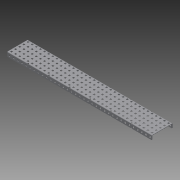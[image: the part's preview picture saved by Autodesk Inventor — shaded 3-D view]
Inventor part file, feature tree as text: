
AUTODESK INVENTOR PART (.ipt)
format: ipt  version: 2015 (Build 190159000, 159)  size: 3,629,568 bytes
history: native  units: in
note: dims shown in document units (in); Inventor stores cm internally (conversion verified against a paired STEP export)
features: other x247, extrude x245, pattern_linear x4, sketch x3, imported_body x1
ambient origin geometry x8: Origin, YZ Plane, XZ Plane, XY Plane, X Axis, Y Axis, Z Axis, Center Point
bodies: Body1 (feature_tree), Body2 (feature_tree), Body3 (feature_tree), Body4 (feature_tree), Body5 (feature_tree), Body6 (feature_tree), Body7 (feature_tree), Body8 (feature_tree), Body9 (feature_tree), Body10 (feature_tree), Body11 (feature_tree), Body12 (feature_tree), Body13 (feature_tree), Body14 (feature_tree), Body15 (feature_tree), Body16 (feature_tree), Body17 (feature_tree), Body18 (feature_tree), Body19 (feature_tree), Body20 (feature_tree), Body21 (feature_tree), Body22 (feature_tree), Body23 (feature_tree), Body24 (feature_tree), Body25 (feature_tree), Body26 (feature_tree), Body27 (feature_tree), Body28 (feature_tree), Body29 (feature_tree), Body30 (feature_tree), Body31 (feature_tree), Body32 (feature_tree), Body33 (feature_tree), Body34 (feature_tree), Body35 (feature_tree), Body36 (feature_tree), Body37 (feature_tree), Body38 (feature_tree), Body39 (feature_tree), Body40 (feature_tree), Body41 (feature_tree), Body42 (feature_tree), Body43 (feature_tree), Body44 (feature_tree), Body45 (feature_tree), Body46 (feature_tree), Body47 (feature_tree), Body48 (feature_tree), Body49 (feature_tree), Body50 (feature_tree), Body51 (feature_tree), Body52 (feature_tree), Body53 (feature_tree), Body54 (feature_tree), Body55 (feature_tree), Body56 (feature_tree), Body57 (feature_tree), Body58 (feature_tree), Body59 (feature_tree), Body60 (feature_tree), Body61 (feature_tree), Body62 (feature_tree), Body63 (feature_tree), Body64 (feature_tree), Body65 (feature_tree), Body66 (feature_tree), Body67 (feature_tree), Body68 (feature_tree), Body69 (feature_tree), Body70 (feature_tree), Body71 (feature_tree), Body72 (feature_tree), Body73 (feature_tree), Body74 (feature_tree), Body75 (feature_tree), Body76 (feature_tree), Body77 (feature_tree), Body78 (feature_tree), Body79 (feature_tree), Body80 (feature_tree), Body81 (feature_tree), Body82 (feature_tree), Body83 (feature_tree), Body84 (feature_tree), Body85 (feature_tree), Body86 (feature_tree), Body87 (feature_tree), Body88 (feature_tree), Body89 (feature_tree), Body90 (feature_tree), Body91 (feature_tree), Body92 (feature_tree), Body93 (feature_tree), Body94 (feature_tree), Body95 (feature_tree), Body96 (feature_tree), Body97 (feature_tree), Body98 (feature_tree), Body99 (feature_tree), Body100 (feature_tree), Body101 (feature_tree), Body102 (feature_tree), Body103 (feature_tree), Body104 (feature_tree), Body105 (feature_tree), Body106 (feature_tree), Body107 (feature_tree), Body108 (feature_tree), Body109 (feature_tree), Body110 (feature_tree), Body111 (feature_tree), Body112 (feature_tree), Body113 (feature_tree), Body114 (feature_tree), Body115 (feature_tree), Body116 (feature_tree), Body117 (feature_tree), Body118 (feature_tree), Body119 (feature_tree), Body120 (feature_tree), Body121 (feature_tree), Body122 (feature_tree), Body123 (feature_tree), Body124 (feature_tree), Body125 (feature_tree), Body126 (feature_tree), Body127 (feature_tree), Body128 (feature_tree), Body129 (feature_tree), Body130 (feature_tree), Body131 (feature_tree), Body132 (feature_tree), Body133 (feature_tree), Body134 (feature_tree), Body135 (feature_tree), Body136 (feature_tree), Body137 (feature_tree), Body138 (feature_tree), Body139 (feature_tree), Body140 (feature_tree), Body141 (feature_tree), Body142 (feature_tree), Body143 (feature_tree), Body144 (feature_tree), Body145 (feature_tree), Body146 (feature_tree), Body147 (feature_tree), Body148 (feature_tree), Body149 (feature_tree), Body150 (feature_tree), Body151 (feature_tree), Body152 (feature_tree), Body153 (feature_tree), Body154 (feature_tree), Body155 (feature_tree), Body156 (feature_tree), Body157 (feature_tree), Body158 (feature_tree), Body159 (feature_tree), Body160 (feature_tree), Body161 (feature_tree), Body162 (feature_tree), Body163 (feature_tree), Body164 (feature_tree), Body165 (feature_tree), Body166 (feature_tree), Body167 (feature_tree), Body168 (feature_tree), Body169 (feature_tree), Body170 (feature_tree), Body171 (feature_tree), Body172 (feature_tree), Body173 (feature_tree), Body174 (feature_tree), Body175 (feature_tree), Body176 (feature_tree), Body177 (feature_tree), Body178 (feature_tree), Body179 (feature_tree), Body180 (feature_tree), Body181 (feature_tree), Body182 (feature_tree), Body183 (feature_tree), Body184 (feature_tree), Body185 (feature_tree), Body186 (feature_tree), Body187 (feature_tree), Body188 (feature_tree), Body189 (feature_tree), Body190 (feature_tree), Body191 (feature_tree), Body192 (feature_tree), Body193 (feature_tree), Body194 (feature_tree), Body195 (feature_tree), Body196 (feature_tree), Body197 (feature_tree), Body198 (feature_tree), Body199 (feature_tree), Body200 (feature_tree), Body201 (feature_tree), Body202 (feature_tree), Body203 (feature_tree), Body204 (feature_tree), Body205 (feature_tree), Body206 (feature_tree), Body207 (feature_tree), Body208 (feature_tree), Body209 (feature_tree), Body210 (feature_tree), Body211 (feature_tree), Body212 (feature_tree), Body213 (feature_tree), Body214 (feature_tree), Body215 (feature_tree), Body216 (feature_tree), Body217 (feature_tree), Body218 (feature_tree), Body219 (feature_tree), Body220 (feature_tree), Body221 (feature_tree), Body222 (feature_tree), Body223 (feature_tree), Body224 (feature_tree), Body225 (feature_tree), Body226 (feature_tree), Body227 (feature_tree), Body228 (feature_tree), Body229 (feature_tree), Body230 (feature_tree), Body231 (feature_tree), Body232 (feature_tree), Body233 (feature_tree), Body234 (feature_tree), Body235 (feature_tree), Body236 (feature_tree), Body237 (feature_tree), Body238 (feature_tree), Body239 (feature_tree), Body240 (feature_tree), Body241 (feature_tree), Body242 (feature_tree), Body243 (feature_tree), Body244 (feature_tree), Body245 (feature_tree), Body246 (feature_tree)
feature tree (500):
  parser-record x1  (decoder bookkeeping rows leaked as tree rows — omitted from the tree; the rows remain in map.json)
  other  "VL-CHAN-151-35 RevA1"
  pattern_linear  "Rectangular Pattern1"  Count1=5 Spacing1=0.5in
  pattern_linear  "Rectangular Pattern2"  Count1=35 Spacing1=0.5in
  pattern_linear  "Rectangular Pattern3"  Spacing1=0.0in  [1 undecoded]
  pattern_linear  "Rectangular Pattern4"  Spacing1=0.0in  [1 undecoded]
  imported_body  "Base1"
  sketch  "Sketch1"  dims[d0=0.05in d1=0.0in]
  other  "Srf1"
  other  "Srf2"
  other  "Srf3"
  other  "Srf4"
  other  "Srf5"
  other  "Srf10"
  other  "Srf15"
  other  "Srf20"
  other  "Srf25"
  other  "Srf30"
  other  "Srf35"
  other  "Srf40"
  other  "Srf45"
  other  "Srf50"
  other  "Srf55"
  other  "Srf60"
  other  "Srf65"
  other  "Srf70"
  other  "Srf75"
  other  "Srf80"
  other  "Srf85"
  other  "Srf90"
  other  "Srf95"
  other  "Srf100"
  other  "Srf105"
  other  "Srf110"
  other  "Srf115"
  other  "Srf120"
  other  "Srf125"
  other  "Srf130"
  other  "Srf135"
  other  "Srf140"
  other  "Srf145"
  other  "Srf150"
  other  "Srf155"
  other  "Srf160"
  other  "Srf165"
  other  "Srf170"
  other  "Srf175"
  other  "Srf6"
  other  "Srf11"
  other  "Srf16"
  other  "Srf21"
  other  "Srf26"
  other  "Srf31"
  other  "Srf36"
  other  "Srf41"
  other  "Srf46"
  other  "Srf51"
  other  "Srf56"
  other  "Srf61"
  other  "Srf66"
  other  "Srf71"
  other  "Srf76"
  other  "Srf81"
  other  "Srf86"
  other  "Srf91"
  other  "Srf96"
  other  "Srf101"
  other  "Srf106"
  other  "Srf111"
  other  "Srf116"
  other  "Srf121"
  other  "Srf126"
  other  "Srf131"
  other  "Srf136"
  other  "Srf141"
  other  "Srf146"
  other  "Srf151"
  other  "Srf156"
  other  "Srf161"
  other  "Srf166"
  other  "Srf171"
  other  "Srf7"
  other  "Srf12"
  other  "Srf17"
  other  "Srf22"
  other  "Srf27"
  other  "Srf32"
  other  "Srf37"
  other  "Srf42"
  other  "Srf47"
  other  "Srf52"
  other  "Srf57"
  other  "Srf62"
  other  "Srf67"
  other  "Srf72"
  other  "Srf77"
  other  "Srf82"
  other  "Srf87"
  other  "Srf92"
  other  "Srf97"
  other  "Srf102"
  other  "Srf107"
  other  "Srf112"
  other  "Srf117"
  other  "Srf122"
  other  "Srf127"
  other  "Srf132"
  other  "Srf137"
  other  "Srf142"
  other  "Srf147"
  other  "Srf152"
  other  "Srf157"
  other  "Srf162"
  other  "Srf167"
  other  "Srf172"
  other  "Srf8"
  other  "Srf13"
  other  "Srf18"
  other  "Srf23"
  other  "Srf28"
  other  "Srf33"
  other  "Srf38"
  other  "Srf43"
  other  "Srf48"
  other  "Srf53"
  other  "Srf58"
  other  "Srf63"
  other  "Srf68"
  other  "Srf73"
  other  "Srf78"
  other  "Srf83"
  other  "Srf88"
  other  "Srf93"
  other  "Srf98"
  other  "Srf103"
  other  "Srf108"
  other  "Srf113"
  other  "Srf118"
  other  "Srf123"
  other  "Srf128"
  other  "Srf133"
  other  "Srf138"
  other  "Srf143"
  other  "Srf148"
  other  "Srf153"
  other  "Srf158"
  other  "Srf163"
  other  "Srf168"
  other  "Srf173"
  other  "Srf9"
  other  "Srf14"
  other  "Srf19"
  other  "Srf24"
  other  "Srf29"
  other  "Srf34"
  other  "Srf39"
  other  "Srf44"
  other  "Srf49"
  other  "Srf54"
  other  "Srf59"
  other  "Srf64"
  other  "Srf69"
  other  "Srf74"
  other  "Srf79"
  other  "Srf84"
  other  "Srf89"
  other  "Srf94"
  other  "Srf99"
  other  "Srf104"
  other  "Srf109"
  other  "Srf114"
  other  "Srf119"
  other  "Srf124"
  other  "Srf129"
  other  "Srf134"
  other  "Srf139"
  other  "Srf144"
  other  "Srf149"
  other  "Srf154"
  other  "Srf159"
  other  "Srf164"
  other  "Srf169"
  other  "Srf174"
  sketch  "Sketch2"  dims[d2=0.0in]
  other  "Srf176"
  other  "Srf177"
  other  "Srf178"
  other  "Srf179"
  other  "Srf180"
  other  "Srf181"
  other  "Srf182"
  other  "Srf183"
  other  "Srf184"
  other  "Srf185"
  other  "Srf186"
  other  "Srf187"
  other  "Srf188"
  other  "Srf189"
  other  "Srf190"
  other  "Srf191"
  other  "Srf192"
  other  "Srf193"
  other  "Srf194"
  other  "Srf195"
  other  "Srf196"
  other  "Srf197"
  other  "Srf198"
  other  "Srf199"
  other  "Srf200"
  other  "Srf201"
  other  "Srf202"
  other  "Srf203"
  other  "Srf204"
  other  "Srf205"
  other  "Srf206"
  other  "Srf207"
  other  "Srf208"
  other  "Srf209"
  other  "Srf210"
  sketch  "Sketch3"  dims[d3=0.0in d4=1.9685in d6=0.5in d7=13.7795in d9=0.5in d10=0.0in d11=0.0in d12=0.0in d13=0.0in d14=0.0in d15=0.0in d16=0.0in d17=0.0in d18=0.0in d19=0.0in d20=0.0in d21=0.0in d22=0.0in d23=0.0in d24=0.0in d25=0.0in d26=0.0in d27=0.0in d28=0.0in d29=0.0in d30=0.0in d31=0.0in d32=0.0in d33=0.0in d34=0.0in d35=0.0in d36=0.0in d37=0.0in d38=0.0in d39=0.0in d40=0.0in d41=0.0in d42=0.0in d43=0.0in d44=0.0in d45=0.0in d46=0.0in d47=0.0in d48=0.0in d49=0.0in d50=0.0in d51=0.0in d52=0.0in d53=0.0in d54=0.0in d55=0.0in d56=0.0in d57=0.0in d58=0.0in d59=0.0in d60=0.0in d61=0.0in d62=0.0in d63=0.0in d64=0.0in d65=0.0in d66=0.0in d67=0.0in d68=0.0in d69=0.0in d70=0.0in d71=0.0in d72=0.0in d73=0.0in d74=0.0in d75=0.0in d76=0.0in d77=0.0in d78=0.0in d79=0.0in d80=0.0in d81=0.0in d82=0.0in d83=0.0in d84=0.0in d85=0.0in d86=0.0in d87=0.0in d88=0.0in d89=0.0in d90=0.0in d91=0.0in d92=0.0in d93=0.0in d94=0.0in d95=0.0in d96=0.0in d97=0.0in d98=0.0in d99=0.0in d100=0.0in d101=0.0in d102=0.0in d103=0.0in d104=0.0in d105=0.0in d106=0.0in d107=0.0in d108=0.0in d109=0.0in d110=0.0in d111=0.0in d112=0.0in d113=0.0in d114=0.0in d115=0.0in d116=0.0in d117=0.0in d118=0.0in d119=0.0in d120=0.0in d121=0.0in d122=0.0in d123=0.0in d124=0.0in d125=0.0in d126=0.0in d127=0.0in d128=0.0in d129=0.0in d130=0.0in d131=0.0in d132=0.0in d133=0.0in d134=0.0in d135=0.0in d136=0.0in d137=0.0in d138=0.0in d139=0.0in d140=0.0in d141=0.0in d142=0.0in d143=0.0in d144=0.0in d145=0.0in d146=0.0in d147=0.0in d148=0.0in d149=0.0in d150=0.0in d151=0.0in d152=0.0in d153=0.0in d154=0.0in d155=0.0in d156=0.0in d157=0.0in d158=0.0in d159=0.0in d160=0.0in d161=0.0in d162=0.0in d163=0.0in d164=0.0in d165=0.0in d166=0.0in d167=0.0in d168=0.0in d169=0.0in d170=0.0in d171=0.0in d172=0.0in d173=0.0in d174=0.0in d175=0.0in d176=0.0in d177=0.0in d178=0.0in d179=0.0in d180=0.0in d181=0.0in d182=0.0in d183=0.0in d184=0.0in d185=0.0in d186=0.0in d187=0.0in d188=0.0in d189=0.0in d190=0.0in d191=0.0in d192=0.0in d193=0.0in d194=0.0in d195=0.0in d196=0.0in d197=0.0in d198=0.0in d199=0.0in d200=0.0in d201=0.0in d202=0.0in d203=0.0in d204=0.0in d205=0.0in d206=0.0in d207=0.0in d208=0.0in d209=0.0in d210=0.0in d211=0.0in d212=0.0in d213=0.0in d214=0.0in d215=0.0in d216=0.0in d217=0.0in d218=0.0in d219=0.0in d220=0.0in d221=0.0in d222=0.0in d223=0.0in d224=0.0in d225=0.0in d226=0.0in d227=0.0in d228=0.0in d229=0.0in d230=0.0in d231=0.0in d232=0.0in d233=0.0in d234=0.0in d235=0.0in d236=0.0in d237=0.0in d238=0.0in d239=0.0in d240=0.0in d241=0.0in d242=0.0in d243=0.0in d244=0.0in d245=0.0in d246=0.0in d247=0.0in d248=0.0in d249=0.0in d250=0.0in d251=0.0in d252=0.0in d253=0.0in d254=0.0in d255=0.0in d256=0.0in d257=0.0in d258=0.0in d259=0.0in d260=0.0in d261=0.0in d262=0.0in d263=0.0in d264=0.0in d265=0.0in d266=0.0in d267=0.0in d268=0.0in d269=0.0in d270=0.0in d271=0.0in d272=0.0in d273=0.0in d274=0.0in d275=0.0in d276=0.0in d277=0.0in d278=0.0in d279=0.0in d280=0.0in d281=0.0in d282=0.0in d283=0.0in d284=0.0in d285=0.0in d286=0.0in d287=0.0in d288=0.0in d289=0.0in d290=0.0in d291=0.0in d292=0.0in d293=0.0in d294=0.0in d295=0.0in d296=0.0in d297=0.0in d298=0.0in d299=0.0in d300=0.0in d301=0.0in d302=0.0in d303=0.0in d304=0.0in d305=0.0in d306=0.0in d307=0.0in d308=0.0in d309=0.0in d310=0.0in d311=0.0in d312=0.0in d313=0.0in d314=0.0in d315=0.0in d316=0.0in d317=0.0in d318=0.0in d319=0.0in d320=0.0in d321=0.0in d322=0.0in d323=0.0in d324=0.0in d325=0.0in d326=0.0in d327=0.0in d328=0.0in d329=0.0in d330=0.0in d331=0.0in d332=0.0in d333=0.0in d334=0.0in d335=0.0in d336=0.0in d337=0.0in d338=0.0in d339=0.0in d340=0.0in d341=0.0in d342=0.0in d343=0.0in d344=0.0in d345=0.0in d346=0.0in d347=0.0in d348=0.0in d349=0.0in d350=0.0in d351=0.0in d352=0.0in d353=0.0in d354=0.0in d355=0.0in d356=0.0in d357=0.05in d358=0.0in d359=13.7795in d361=0.5in d362=0.0in d363=0.0in d364=0.0in d365=0.0in d366=0.0in d367=0.0in d368=0.0in d369=0.0in d370=0.0in d371=0.0in d372=0.0in d373=0.0in d374=0.0in d375=0.0in d376=0.0in d377=0.0in d378=0.0in d379=0.0in d380=0.0in d381=0.0in d382=0.0in d383=0.0in d384=0.0in d385=0.0in d386=0.0in d387=0.0in d388=0.0in d389=0.0in d390=0.0in d391=0.0in d392=0.0in d393=0.0in d394=0.0in d395=0.0in d396=0.0in d397=0.0in d398=0.0in d399=0.0in d400=0.0in d401=0.0in d402=0.0in d403=0.0in d404=0.0in d405=0.0in d406=0.0in d407=0.0in d408=0.0in d409=0.0in d410=0.0in d411=0.0in d412=0.0in d413=0.0in d414=0.0in d415=0.0in d416=0.0in d417=0.0in d418=0.0in d419=0.0in d420=0.0in d421=0.0in d422=0.0in d423=0.0in d424=0.0in d425=0.0in d426=0.0in d427=0.0in d428=0.0in d429=0.0in d430=0.0in d431=0.0in d432=0.05in d433=0.0in d434=13.7795in d436=0.5in d437=0.0in d438=0.0in d439=0.0in d440=0.0in d441=0.0in d442=0.0in d443=0.0in d444=0.0in d445=0.0in d446=0.0in d447=0.0in d448=0.0in d449=0.0in d450=0.0in d451=0.0in d452=0.0in d453=0.0in d454=0.0in d455=0.0in d456=0.0in d457=0.0in d458=0.0in d459=0.0in d460=0.0in d461=0.0in d462=0.0in d463=0.0in d464=0.0in d465=0.0in d466=0.0in d467=0.0in d468=0.0in d469=0.0in d470=0.0in d471=0.0in d472=0.0in d473=0.0in d474=0.0in d475=0.0in d476=0.0in d477=0.0in d478=0.0in d479=0.0in d480=0.0in d481=0.0in d482=0.0in d483=0.0in d484=0.0in d485=0.0in d486=0.0in d487=0.0in d488=0.0in d489=0.0in d490=0.0in d491=0.0in d492=0.0in d493=0.0in d494=0.0in d495=0.0in d496=0.0in d497=0.0in d498=0.0in d499=0.0in d500=0.0in d501=0.0in d502=0.0in d503=0.0in d504=0.0in d505=0.0in d506=0.0in]
  other  "Srf211"
  other  "Srf212"
  other  "Srf213"
  other  "Srf214"
  other  "Srf215"
  other  "Srf216"
  other  "Srf217"
  other  "Srf218"
  other  "Srf219"
  other  "Srf220"
  other  "Srf221"
  other  "Srf222"
  other  "Srf223"
  other  "Srf224"
  other  "Srf225"
  other  "Srf226"
  other  "Srf227"
  other  "Srf228"
  other  "Srf229"
  other  "Srf230"
  other  "Srf231"
  other  "Srf232"
  other  "Srf233"
  other  "Srf234"
  other  "Srf235"
  other  "Srf236"
  other  "Srf237"
  other  "Srf238"
  other  "Srf239"
  other  "Srf240"
  other  "Srf241"
  other  "Srf242"
  other  "Srf243"
  other  "Srf244"
  other  "Srf245"
  extrude  "ExtrusionSrf1"  TaperAngle=0.0deg  [1 undecoded]
  extrude  "ExtrusionSrf176"  TaperAngle=0.0deg  [1 undecoded]
  extrude  "ExtrusionSrf211"  TaperAngle=0.0deg  [1 undecoded]
  extrude  "ExtrusionSrf2"  TaperAngle=0.0deg  [1 undecoded]
  extrude  "ExtrusionSrf3"  TaperAngle=0.0deg  [1 undecoded]
  extrude  "ExtrusionSrf4"  TaperAngle=0.0deg  [1 undecoded]
  extrude  "ExtrusionSrf5"  TaperAngle=0.0deg  [1 undecoded]
  extrude  "ExtrusionSrf6"  TaperAngle=0.0deg  [1 undecoded]
  extrude  "ExtrusionSrf7"  TaperAngle=0.0deg  [1 undecoded]
  extrude  "ExtrusionSrf8"  TaperAngle=0.0deg  [1 undecoded]
  extrude  "ExtrusionSrf9"  TaperAngle=0.0deg  [1 undecoded]
  extrude  "ExtrusionSrf10"  TaperAngle=0.0deg  [1 undecoded]
  extrude  "ExtrusionSrf11"  TaperAngle=0.0deg  [1 undecoded]
  extrude  "ExtrusionSrf12"  TaperAngle=0.0deg  [1 undecoded]
  extrude  "ExtrusionSrf13"  TaperAngle=0.0deg  [1 undecoded]
  extrude  "ExtrusionSrf14"  TaperAngle=0.0deg  [1 undecoded]
  extrude  "ExtrusionSrf15"  TaperAngle=0.0deg  [1 undecoded]
  extrude  "ExtrusionSrf16"  TaperAngle=0.0deg  [1 undecoded]
  extrude  "ExtrusionSrf17"  TaperAngle=0.0deg  [1 undecoded]
  extrude  "ExtrusionSrf18"  TaperAngle=0.0deg  [1 undecoded]
  extrude  "ExtrusionSrf19"  TaperAngle=0.0deg  [1 undecoded]
  extrude  "ExtrusionSrf20"  TaperAngle=0.0deg  [1 undecoded]
  extrude  "ExtrusionSrf21"  TaperAngle=0.0deg  [1 undecoded]
  extrude  "ExtrusionSrf22"  TaperAngle=0.0deg  [1 undecoded]
  extrude  "ExtrusionSrf23"  TaperAngle=0.0deg  [1 undecoded]
  extrude  "ExtrusionSrf24"  TaperAngle=0.0deg  [1 undecoded]
  extrude  "ExtrusionSrf25"  TaperAngle=0.0deg  [1 undecoded]
  extrude  "ExtrusionSrf26"  TaperAngle=0.0deg  [1 undecoded]
  extrude  "ExtrusionSrf27"  TaperAngle=0.0deg  [1 undecoded]
  extrude  "ExtrusionSrf28"  TaperAngle=0.0deg  [1 undecoded]
  extrude  "ExtrusionSrf29"  TaperAngle=0.0deg  [1 undecoded]
  extrude  "ExtrusionSrf30"  TaperAngle=0.0deg  [1 undecoded]
  extrude  "ExtrusionSrf31"  TaperAngle=0.0deg  [1 undecoded]
  extrude  "ExtrusionSrf32"  TaperAngle=0.0deg  [1 undecoded]
  extrude  "ExtrusionSrf33"  TaperAngle=0.0deg  [1 undecoded]
  extrude  "ExtrusionSrf34"  TaperAngle=0.0deg  [1 undecoded]
  extrude  "ExtrusionSrf35"  TaperAngle=0.0deg  [1 undecoded]
  extrude  "ExtrusionSrf36"  TaperAngle=0.0deg  [1 undecoded]
  extrude  "ExtrusionSrf37"  TaperAngle=0.0deg  [1 undecoded]
  extrude  "ExtrusionSrf38"  TaperAngle=0.0deg  [1 undecoded]
  extrude  "ExtrusionSrf39"  TaperAngle=0.0deg  [1 undecoded]
  extrude  "ExtrusionSrf40"  TaperAngle=0.0deg  [1 undecoded]
  extrude  "ExtrusionSrf41"  TaperAngle=0.0deg  [1 undecoded]
  extrude  "ExtrusionSrf42"  TaperAngle=0.0deg  [1 undecoded]
  extrude  "ExtrusionSrf43"  TaperAngle=0.0deg  [1 undecoded]
  extrude  "ExtrusionSrf44"  TaperAngle=0.0deg  [1 undecoded]
  extrude  "ExtrusionSrf45"  TaperAngle=0.0deg  [1 undecoded]
  extrude  "ExtrusionSrf46"  TaperAngle=0.0deg  [1 undecoded]
  extrude  "ExtrusionSrf47"  TaperAngle=0.0deg  [1 undecoded]
  extrude  "ExtrusionSrf48"  TaperAngle=0.0deg  [1 undecoded]
  extrude  "ExtrusionSrf49"  TaperAngle=0.0deg  [1 undecoded]
  extrude  "ExtrusionSrf50"  TaperAngle=0.0deg  [1 undecoded]
  extrude  "ExtrusionSrf51"  TaperAngle=0.0deg  [1 undecoded]
  extrude  "ExtrusionSrf52"  TaperAngle=0.0deg  [1 undecoded]
  extrude  "ExtrusionSrf53"  TaperAngle=0.0deg  [1 undecoded]
  extrude  "ExtrusionSrf54"  TaperAngle=0.0deg  [1 undecoded]
  extrude  "ExtrusionSrf55"  TaperAngle=0.0deg  [1 undecoded]
  extrude  "ExtrusionSrf56"  TaperAngle=0.0deg  [1 undecoded]
  extrude  "ExtrusionSrf57"  TaperAngle=0.0deg  [1 undecoded]
  extrude  "ExtrusionSrf58"  TaperAngle=0.0deg  [1 undecoded]
  extrude  "ExtrusionSrf59"  TaperAngle=0.0deg  [1 undecoded]
  extrude  "ExtrusionSrf60"  TaperAngle=0.0deg  [1 undecoded]
  extrude  "ExtrusionSrf61"  TaperAngle=0.0deg  [1 undecoded]
  extrude  "ExtrusionSrf62"  TaperAngle=0.0deg  [1 undecoded]
  extrude  "ExtrusionSrf63"  TaperAngle=0.0deg  [1 undecoded]
  extrude  "ExtrusionSrf64"  TaperAngle=0.0deg  [1 undecoded]
  extrude  "ExtrusionSrf65"  TaperAngle=0.0deg  [1 undecoded]
  extrude  "ExtrusionSrf66"  TaperAngle=0.0deg  [1 undecoded]
  extrude  "ExtrusionSrf67"  TaperAngle=0.0deg  [1 undecoded]
  extrude  "ExtrusionSrf68"  TaperAngle=0.0deg  [1 undecoded]
  extrude  "ExtrusionSrf69"  TaperAngle=0.0deg  [1 undecoded]
  extrude  "ExtrusionSrf70"  TaperAngle=0.0deg  [1 undecoded]
  extrude  "ExtrusionSrf71"  TaperAngle=0.0deg  [1 undecoded]
  extrude  "ExtrusionSrf72"  TaperAngle=0.0deg  [1 undecoded]
  extrude  "ExtrusionSrf73"  TaperAngle=0.0deg  [1 undecoded]
  extrude  "ExtrusionSrf74"  TaperAngle=0.0deg  [1 undecoded]
  extrude  "ExtrusionSrf75"  TaperAngle=0.0deg  [1 undecoded]
  extrude  "ExtrusionSrf76"  TaperAngle=0.0deg  [1 undecoded]
  extrude  "ExtrusionSrf77"  TaperAngle=0.0deg  [1 undecoded]
  extrude  "ExtrusionSrf78"  TaperAngle=0.0deg  [1 undecoded]
  extrude  "ExtrusionSrf79"  TaperAngle=0.0deg  [1 undecoded]
  extrude  "ExtrusionSrf80"  TaperAngle=0.0deg  [1 undecoded]
  extrude  "ExtrusionSrf81"  TaperAngle=0.0deg  [1 undecoded]
  extrude  "ExtrusionSrf82"  TaperAngle=0.0deg  [1 undecoded]
  extrude  "ExtrusionSrf83"  TaperAngle=0.0deg  [1 undecoded]
  extrude  "ExtrusionSrf84"  TaperAngle=0.0deg  [1 undecoded]
  extrude  "ExtrusionSrf85"  TaperAngle=0.0deg  [1 undecoded]
  extrude  "ExtrusionSrf86"  TaperAngle=0.0deg  [1 undecoded]
  extrude  "ExtrusionSrf87"  TaperAngle=0.0deg  [1 undecoded]
  extrude  "ExtrusionSrf88"  TaperAngle=0.0deg  [1 undecoded]
  extrude  "ExtrusionSrf89"  TaperAngle=0.0deg  [1 undecoded]
  extrude  "ExtrusionSrf90"  TaperAngle=0.0deg  [1 undecoded]
  extrude  "ExtrusionSrf91"  TaperAngle=0.0deg  [1 undecoded]
  extrude  "ExtrusionSrf92"  TaperAngle=0.0deg  [1 undecoded]
  extrude  "ExtrusionSrf93"  TaperAngle=0.0deg  [1 undecoded]
  extrude  "ExtrusionSrf94"  TaperAngle=0.0deg  [1 undecoded]
  extrude  "ExtrusionSrf95"  TaperAngle=0.0deg  [1 undecoded]
  extrude  "ExtrusionSrf96"  TaperAngle=0.0deg  [1 undecoded]
  extrude  "ExtrusionSrf97"  TaperAngle=0.0deg  [1 undecoded]
  extrude  "ExtrusionSrf98"  TaperAngle=0.0deg  [1 undecoded]
  extrude  "ExtrusionSrf99"  TaperAngle=0.0deg  [1 undecoded]
  extrude  "ExtrusionSrf100"  TaperAngle=0.0deg  [1 undecoded]
  extrude  "ExtrusionSrf101"  TaperAngle=0.0deg  [1 undecoded]
  extrude  "ExtrusionSrf102"  TaperAngle=0.0deg  [1 undecoded]
  extrude  "ExtrusionSrf103"  TaperAngle=0.0deg  [1 undecoded]
  extrude  "ExtrusionSrf104"  TaperAngle=0.0deg  [1 undecoded]
  extrude  "ExtrusionSrf105"  TaperAngle=0.0deg  [1 undecoded]
  extrude  "ExtrusionSrf106"  TaperAngle=0.0deg  [1 undecoded]
  extrude  "ExtrusionSrf107"  TaperAngle=0.0deg  [1 undecoded]
  extrude  "ExtrusionSrf108"  TaperAngle=0.0deg  [1 undecoded]
  extrude  "ExtrusionSrf109"  TaperAngle=0.0deg  [1 undecoded]
  extrude  "ExtrusionSrf110"  TaperAngle=0.0deg  [1 undecoded]
  extrude  "ExtrusionSrf111"  TaperAngle=0.0deg  [1 undecoded]
  extrude  "ExtrusionSrf112"  TaperAngle=0.0deg  [1 undecoded]
  extrude  "ExtrusionSrf113"  TaperAngle=0.0deg  [1 undecoded]
  extrude  "ExtrusionSrf114"  TaperAngle=0.0deg  [1 undecoded]
  extrude  "ExtrusionSrf115"  TaperAngle=0.0deg  [1 undecoded]
  extrude  "ExtrusionSrf116"  TaperAngle=0.0deg  [1 undecoded]
  extrude  "ExtrusionSrf117"  TaperAngle=0.0deg  [1 undecoded]
  extrude  "ExtrusionSrf118"  TaperAngle=0.0deg  [1 undecoded]
  extrude  "ExtrusionSrf119"  TaperAngle=0.0deg  [1 undecoded]
  extrude  "ExtrusionSrf120"  TaperAngle=0.0deg  [1 undecoded]
  extrude  "ExtrusionSrf121"  TaperAngle=0.0deg  [1 undecoded]
  extrude  "ExtrusionSrf122"  TaperAngle=0.0deg  [1 undecoded]
  extrude  "ExtrusionSrf123"  TaperAngle=0.0deg  [1 undecoded]
  extrude  "ExtrusionSrf124"  TaperAngle=0.0deg  [1 undecoded]
  extrude  "ExtrusionSrf125"  TaperAngle=0.0deg  [1 undecoded]
  extrude  "ExtrusionSrf126"  TaperAngle=0.0deg  [1 undecoded]
  extrude  "ExtrusionSrf127"  TaperAngle=0.0deg  [1 undecoded]
  extrude  "ExtrusionSrf128"  TaperAngle=0.0deg  [1 undecoded]
  extrude  "ExtrusionSrf129"  TaperAngle=0.0deg  [1 undecoded]
  extrude  "ExtrusionSrf130"  TaperAngle=0.0deg  [1 undecoded]
  extrude  "ExtrusionSrf131"  TaperAngle=0.0deg  [1 undecoded]
  extrude  "ExtrusionSrf132"  TaperAngle=0.0deg  [1 undecoded]
  extrude  "ExtrusionSrf133"  TaperAngle=0.0deg  [1 undecoded]
  extrude  "ExtrusionSrf134"  TaperAngle=0.0deg  [1 undecoded]
  extrude  "ExtrusionSrf135"  TaperAngle=0.0deg  [1 undecoded]
  extrude  "ExtrusionSrf136"  TaperAngle=0.0deg  [1 undecoded]
  extrude  "ExtrusionSrf137"  TaperAngle=0.0deg  [1 undecoded]
  extrude  "ExtrusionSrf138"  TaperAngle=0.0deg  [1 undecoded]
  extrude  "ExtrusionSrf139"  TaperAngle=0.0deg  [1 undecoded]
  extrude  "ExtrusionSrf140"  TaperAngle=0.0deg  [1 undecoded]
  extrude  "ExtrusionSrf141"  TaperAngle=0.0deg  [1 undecoded]
  extrude  "ExtrusionSrf142"  TaperAngle=0.0deg  [1 undecoded]
  extrude  "ExtrusionSrf143"  TaperAngle=0.0deg  [1 undecoded]
  extrude  "ExtrusionSrf144"  TaperAngle=0.0deg  [1 undecoded]
  extrude  "ExtrusionSrf145"  TaperAngle=0.0deg  [1 undecoded]
  extrude  "ExtrusionSrf146"  TaperAngle=0.0deg  [1 undecoded]
  extrude  "ExtrusionSrf147"  TaperAngle=0.0deg  [1 undecoded]
  extrude  "ExtrusionSrf148"  TaperAngle=0.0deg  [1 undecoded]
  extrude  "ExtrusionSrf149"  TaperAngle=0.0deg  [1 undecoded]
  extrude  "ExtrusionSrf150"  TaperAngle=0.0deg  [1 undecoded]
  extrude  "ExtrusionSrf151"  TaperAngle=0.0deg  [1 undecoded]
  extrude  "ExtrusionSrf152"  TaperAngle=0.0deg  [1 undecoded]
  extrude  "ExtrusionSrf153"  TaperAngle=0.0deg  [1 undecoded]
  extrude  "ExtrusionSrf154"  TaperAngle=0.0deg  [1 undecoded]
  extrude  "ExtrusionSrf155"  TaperAngle=0.0deg  [1 undecoded]
  extrude  "ExtrusionSrf156"  TaperAngle=0.0deg  [1 undecoded]
  extrude  "ExtrusionSrf157"  TaperAngle=0.0deg  [1 undecoded]
  extrude  "ExtrusionSrf158"  TaperAngle=0.0deg  [1 undecoded]
  extrude  "ExtrusionSrf159"  TaperAngle=0.0deg  [1 undecoded]
  extrude  "ExtrusionSrf160"  TaperAngle=0.0deg  [1 undecoded]
  extrude  "ExtrusionSrf161"  TaperAngle=0.0deg  [1 undecoded]
  extrude  "ExtrusionSrf162"  TaperAngle=0.0deg  [1 undecoded]
  extrude  "ExtrusionSrf163"  TaperAngle=0.0deg  [1 undecoded]
  extrude  "ExtrusionSrf164"  TaperAngle=0.0deg  [1 undecoded]
  extrude  "ExtrusionSrf165"  TaperAngle=0.0deg  [1 undecoded]
  extrude  "ExtrusionSrf166"  TaperAngle=0.0deg  [1 undecoded]
  extrude  "ExtrusionSrf167"  TaperAngle=0.0deg  [1 undecoded]
  extrude  "ExtrusionSrf168"  TaperAngle=0.0deg  [1 undecoded]
  extrude  "ExtrusionSrf169"  TaperAngle=0.0deg  [1 undecoded]
  extrude  "ExtrusionSrf170"  TaperAngle=0.0deg  [1 undecoded]
  extrude  "ExtrusionSrf171"  TaperAngle=0.0deg  [1 undecoded]
  extrude  "ExtrusionSrf172"  TaperAngle=0.0deg  [1 undecoded]
  extrude  "ExtrusionSrf173"  TaperAngle=0.0deg  [1 undecoded]
  extrude  "ExtrusionSrf174"  TaperAngle=0.0deg  [1 undecoded]
  extrude  "ExtrusionSrf175"  TaperAngle=0.0deg  [1 undecoded]
  extrude  "ExtrusionSrf177"  TaperAngle=0.0deg  [1 undecoded]
  extrude  "ExtrusionSrf178"  TaperAngle=0.0deg  [1 undecoded]
  extrude  "ExtrusionSrf179"  TaperAngle=0.0deg  [1 undecoded]
  extrude  "ExtrusionSrf180"  TaperAngle=0.0deg  [1 undecoded]
  extrude  "ExtrusionSrf181"  TaperAngle=0.0deg  [1 undecoded]
  extrude  "ExtrusionSrf182"  TaperAngle=0.0deg  [1 undecoded]
  extrude  "ExtrusionSrf183"  TaperAngle=0.0deg  [1 undecoded]
  extrude  "ExtrusionSrf184"  TaperAngle=0.0deg  [1 undecoded]
  extrude  "ExtrusionSrf185"  TaperAngle=0.0deg  [1 undecoded]
  extrude  "ExtrusionSrf186"  TaperAngle=0.0deg  [1 undecoded]
  extrude  "ExtrusionSrf187"  TaperAngle=0.0deg  [1 undecoded]
  extrude  "ExtrusionSrf188"  TaperAngle=0.0deg  [1 undecoded]
  extrude  "ExtrusionSrf189"  TaperAngle=0.0deg  [1 undecoded]
  extrude  "ExtrusionSrf190"  TaperAngle=0.0deg  [1 undecoded]
  extrude  "ExtrusionSrf191"  TaperAngle=0.0deg  [1 undecoded]
  extrude  "ExtrusionSrf192"  TaperAngle=0.0deg  [1 undecoded]
  extrude  "ExtrusionSrf193"  TaperAngle=0.0deg  [1 undecoded]
  extrude  "ExtrusionSrf194"  TaperAngle=0.0deg  [1 undecoded]
  extrude  "ExtrusionSrf195"  TaperAngle=0.0deg  [1 undecoded]
  extrude  "ExtrusionSrf196"  TaperAngle=0.0deg  [1 undecoded]
  extrude  "ExtrusionSrf197"  TaperAngle=0.0deg  [1 undecoded]
  extrude  "ExtrusionSrf198"  TaperAngle=0.0deg  [1 undecoded]
  extrude  "ExtrusionSrf199"  TaperAngle=0.0deg  [1 undecoded]
  extrude  "ExtrusionSrf200"  TaperAngle=0.0deg  [1 undecoded]
  extrude  "ExtrusionSrf201"  TaperAngle=0.0deg  [1 undecoded]
  extrude  "ExtrusionSrf202"  TaperAngle=0.0deg  [1 undecoded]
  extrude  "ExtrusionSrf203"  TaperAngle=0.0deg  [1 undecoded]
  extrude  "ExtrusionSrf204"  TaperAngle=0.0deg  [1 undecoded]
  extrude  "ExtrusionSrf205"  TaperAngle=0.0deg  [1 undecoded]
  extrude  "ExtrusionSrf206"  TaperAngle=0.0deg  [1 undecoded]
  extrude  "ExtrusionSrf207"  TaperAngle=0.0deg  [1 undecoded]
  extrude  "ExtrusionSrf208"  TaperAngle=0.0deg  [1 undecoded]
  extrude  "ExtrusionSrf209"  TaperAngle=0.0deg  [1 undecoded]
  extrude  "ExtrusionSrf210"  TaperAngle=0.0deg  [1 undecoded]
  extrude  "ExtrusionSrf212"  TaperAngle=0.0deg  [1 undecoded]
  extrude  "ExtrusionSrf213"  TaperAngle=0.0deg  [1 undecoded]
  extrude  "ExtrusionSrf214"  TaperAngle=0.0deg  [1 undecoded]
  extrude  "ExtrusionSrf215"  TaperAngle=0.0deg  [1 undecoded]
  extrude  "ExtrusionSrf216"  TaperAngle=0.0deg  [1 undecoded]
  extrude  "ExtrusionSrf217"  TaperAngle=0.0deg  [1 undecoded]
  extrude  "ExtrusionSrf218"  TaperAngle=0.0deg  [1 undecoded]
  extrude  "ExtrusionSrf219"  TaperAngle=0.0deg  [1 undecoded]
  extrude  "ExtrusionSrf220"  TaperAngle=0.0deg  [1 undecoded]
  extrude  "ExtrusionSrf221"  TaperAngle=0.0deg  [1 undecoded]
  extrude  "ExtrusionSrf222"  TaperAngle=0.0deg  [1 undecoded]
  extrude  "ExtrusionSrf223"  TaperAngle=0.0deg  [1 undecoded]
  extrude  "ExtrusionSrf224"  TaperAngle=0.0deg  [1 undecoded]
  extrude  "ExtrusionSrf225"  TaperAngle=0.0deg  [1 undecoded]
  extrude  "ExtrusionSrf226"  TaperAngle=0.0deg  [1 undecoded]
  extrude  "ExtrusionSrf227"  TaperAngle=0.0deg  [1 undecoded]
  extrude  "ExtrusionSrf228"  TaperAngle=0.0deg  [1 undecoded]
  extrude  "ExtrusionSrf229"  TaperAngle=0.0deg  [1 undecoded]
  extrude  "ExtrusionSrf230"  TaperAngle=0.0deg  [1 undecoded]
  extrude  "ExtrusionSrf231"  TaperAngle=0.0deg  [1 undecoded]
  extrude  "ExtrusionSrf232"  TaperAngle=0.0deg  [1 undecoded]
  extrude  "ExtrusionSrf233"  TaperAngle=0.0deg  [1 undecoded]
  extrude  "ExtrusionSrf234"  TaperAngle=0.0deg  [1 undecoded]
  extrude  "ExtrusionSrf235"  TaperAngle=0.0deg  [1 undecoded]
  extrude  "ExtrusionSrf236"  TaperAngle=0.0deg  [1 undecoded]
  extrude  "ExtrusionSrf237"  TaperAngle=0.0deg  [1 undecoded]
  extrude  "ExtrusionSrf238"  TaperAngle=0.0deg  [1 undecoded]
  extrude  "ExtrusionSrf239"  TaperAngle=0.0deg  [1 undecoded]
  extrude  "ExtrusionSrf240"  TaperAngle=0.0deg  [1 undecoded]
  extrude  "ExtrusionSrf241"  TaperAngle=0.0deg  [1 undecoded]
  extrude  "ExtrusionSrf242"  TaperAngle=0.0deg  [1 undecoded]
  extrude  "ExtrusionSrf243"  TaperAngle=0.0deg  [1 undecoded]
  extrude  "ExtrusionSrf244"  TaperAngle=0.0deg  [1 undecoded]
  extrude  "ExtrusionSrf245"  TaperAngle=0.0deg  [1 undecoded]
note: 247 required parameter values undecoded (feature->parameter linkage not recoverable at this tier; creation-order binding heuristic only, values carry confidence <= 0.55)
